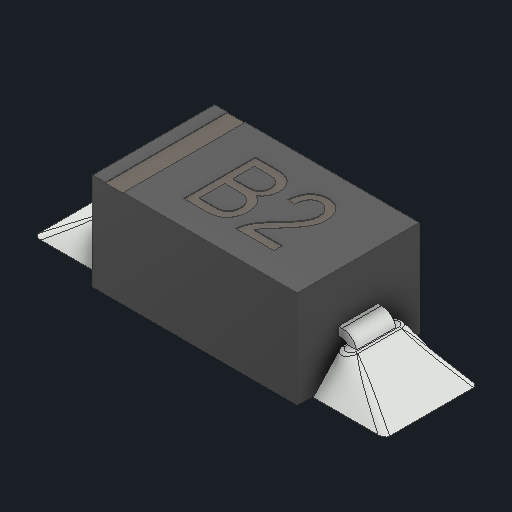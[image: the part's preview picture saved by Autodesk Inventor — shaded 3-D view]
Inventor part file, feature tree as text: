
AUTODESK INVENTOR PART (.ipt)
format: ipt  version: 2023 (Build 270158000, 158)  size: 336,896 bytes
history: native  units: in
note: dims shown in document units (in); Inventor stores cm internally (conversion verified against a paired STEP export)
features: fillet x1
ambient origin geometry x8: Origin, YZ Plane, XZ Plane, XY Plane, X Axis, Y Axis, Z Axis, Center Point
bodies: Solid1 (feature_tree)
feature tree (1):
  fillet  "Fillet9"  [1 undecoded]
note: 1 required parameter value undecoded (feature->parameter linkage not recoverable at this tier; creation-order binding heuristic only, values carry confidence <= 0.55)
